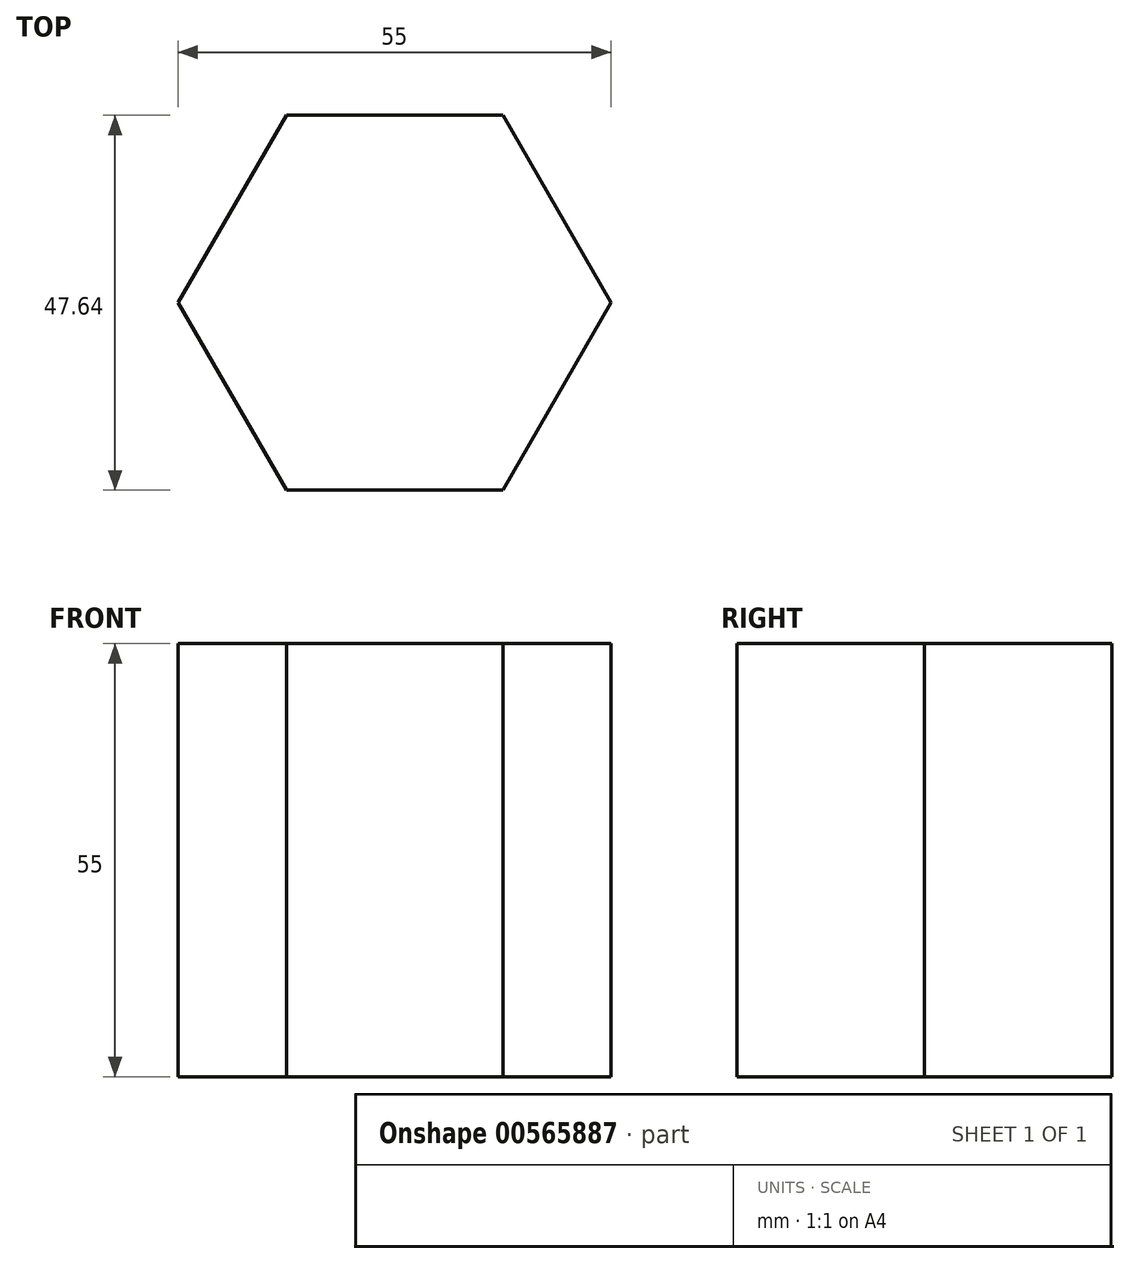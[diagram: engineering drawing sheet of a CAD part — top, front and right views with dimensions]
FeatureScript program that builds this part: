
annotation { "Feature Type Name" : "Feature", "Feature Type Description" : "" }
export const myFeature = defineFeature(function(context is Context, id is Id, definition is map)
    precondition{}
    {
        {
            var Q0;
            Q0=qCreatedBy(makeId("Top.planeOp"),FACE);
            var sketch = newSketch(context, id + "F0", { "sketchPlane" : qUnion([Q0])});
            skLineSegment(sketch, "E0", {"start": v(0, 0) * mm, "end": v(27.5, 0) * mm});
            skCircle(sketch, "E1.cCircle", {"center": v(0, 0) * mm, "radius": 27.5 * mm, "construction": true});
            skLineSegment(sketch, "E1.0", {"start": v(27.5, 0) * mm, "end": v(13.75, -23.82) * mm});
            skLineSegment(sketch, "E1.1", {"start": v(13.75, -23.82) * mm, "end": v(-13.75, -23.82) * mm});
            skLineSegment(sketch, "E1.2", {"start": v(-13.75, -23.82) * mm, "end": v(-27.5, 0) * mm});
            skLineSegment(sketch, "E1.3", {"start": v(-27.5, 0) * mm, "end": v(-13.75, 23.82) * mm});
            skLineSegment(sketch, "E1.4", {"start": v(-13.75, 23.82) * mm, "end": v(13.75, 23.82) * mm});
            skLineSegment(sketch, "E1.5", {"start": v(13.75, 23.82) * mm, "end": v(27.5, 0) * mm});
            skSolve(sketch);
        }
        {
            var Q0;
            Q0 = qSketchRegion(id + "F0", true);
            extrude(context, id + "F1", {"entities" : qUnion([Q0]), "depth" : 55 * mm, "offsetDistance" : 25 * mm});
        }
    });
